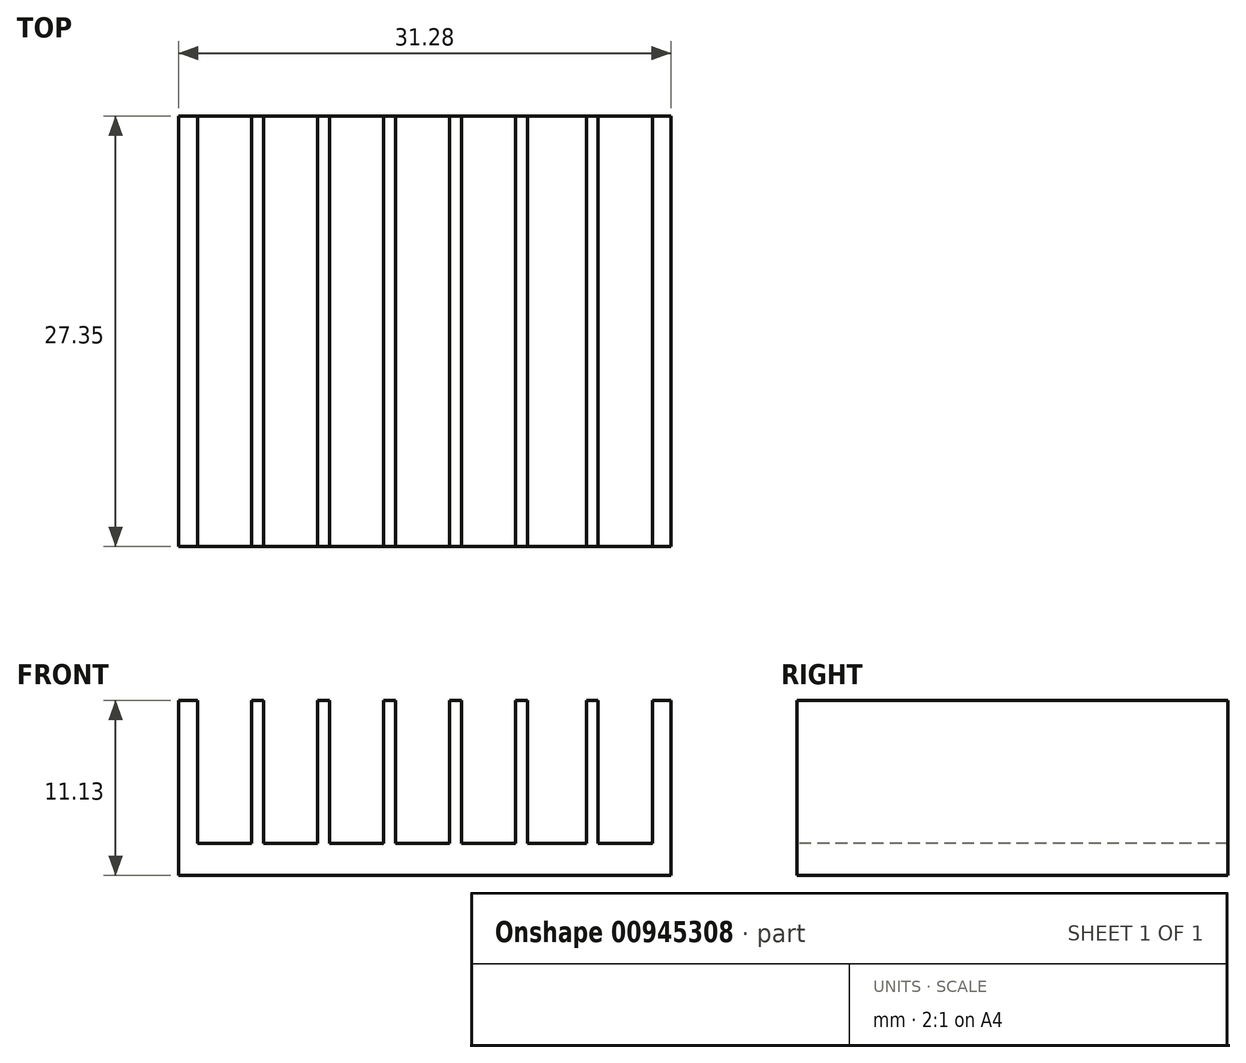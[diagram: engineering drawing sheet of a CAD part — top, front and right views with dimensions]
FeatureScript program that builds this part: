
annotation { "Feature Type Name" : "Feature", "Feature Type Description" : "" }
export const myFeature = defineFeature(function(context is Context, id is Id, definition is map)
    precondition{}
    {
        {
            var Q0;
            Q0=qCreatedBy(makeId("Top.planeOp"),FACE);
            var sketch = newSketch(context, id + "F0", { "sketchPlane" : qUnion([Q0])});
            skLineSegment(sketch, "E0", {"start": v(-31.28, 27.35) * mm, "end": v(0, 27.35) * mm});
            skLineSegment(sketch, "E1", {"start": v(0, 27.35) * mm, "end": v(0, 0) * mm});
            skLineSegment(sketch, "E2", {"start": v(0, 0) * mm, "end": v(-31.28, 0) * mm});
            skLineSegment(sketch, "E3", {"start": v(-31.28, 0) * mm, "end": v(-31.28, 27.35) * mm});
            skSolve(sketch);
        }
        {
            var Q0;
            Q0=makeQuery(id+"F0.imprint","IMPRINT",FACE,{"disambiguationData":[TD([[makeQuery(id+"F0.imprint","IMPRINT",EDGE,{"derivedFrom":sQuery(id+"F0.wireOp",EDGE,"E0")}),-1.0]])]});
            extrude(context, id + "F1", {"entities" : qUnion([Q0]), "depth" : 11.13 * mm, "offsetDistance" : 25.4 * mm});
        }
        {
            var Q0;
            Q0=makeQuery(id+"F1.opExtrude","SWEPT_FACE",FACE,{"disambiguationData":[OSD([sQuery(id+"F0.wireOp",EDGE,"E2")])]});
            var sketch = newSketch(context, id + "F2", { "sketchPlane" : qUnion([Q0])});
            skLineSegment(sketch, "E4", {"start": v(-30.09, 11.13) * mm, "end": v(-30.09, 2.04) * mm});
            skLineSegment(sketch, "E5", {"start": v(-30.09, 2.04) * mm, "end": v(-26.63, 2.04) * mm});
            skLineSegment(sketch, "E6", {"start": v(-26.63, 2.04) * mm, "end": v(-26.63, 11.13) * mm});
            skLineSegment(sketch, "E7", {"start": v(-1.2, 11.13) * mm, "end": v(-1.2, 2.04) * mm});
            skLineSegment(sketch, "E8", {"start": v(-1.2, 2.04) * mm, "end": v(-4.65, 2.04) * mm});
            skLineSegment(sketch, "E9", {"start": v(-4.65, 2.04) * mm, "end": v(-4.65, 11.13) * mm});
            skLineSegment(sketch, "E10", {"start": v(-25.9, 11.13) * mm, "end": v(-25.9, 2.03) * mm});
            skLineSegment(sketch, "E11", {"start": v(-25.9, 2.03) * mm, "end": v(-22.44, 2.03) * mm});
            skLineSegment(sketch, "E12", {"start": v(-22.44, 2.03) * mm, "end": v(-22.44, 11.13) * mm});
            skLineSegment(sketch, "E13", {"start": v(-21.7, 11.13) * mm, "end": v(-21.7, 2.03) * mm});
            skLineSegment(sketch, "E14", {"start": v(-21.7, 2.03) * mm, "end": v(-18.25, 2.03) * mm});
            skLineSegment(sketch, "E15", {"start": v(-18.25, 2.03) * mm, "end": v(-18.25, 11.13) * mm});
            skLineSegment(sketch, "E16", {"start": v(-17.51, 11.13) * mm, "end": v(-17.51, 2.03) * mm});
            skLineSegment(sketch, "E17", {"start": v(-17.51, 2.03) * mm, "end": v(-14.06, 2.03) * mm});
            skLineSegment(sketch, "E18", {"start": v(-14.06, 2.03) * mm, "end": v(-14.06, 11.13) * mm});
            skLineSegment(sketch, "E19", {"start": v(-13.32, 11.13) * mm, "end": v(-13.32, 2.03) * mm});
            skLineSegment(sketch, "E20", {"start": v(-13.32, 2.03) * mm, "end": v(-9.87, 2.03) * mm});
            skLineSegment(sketch, "E21", {"start": v(-9.87, 2.03) * mm, "end": v(-9.87, 11.13) * mm});
            skLineSegment(sketch, "E22", {"start": v(-9.13, 11.13) * mm, "end": v(-9.13, 2.03) * mm});
            skLineSegment(sketch, "E23", {"start": v(-9.13, 2.03) * mm, "end": v(-5.38, 2.03) * mm});
            skLineSegment(sketch, "E24", {"start": v(-5.38, 2.03) * mm, "end": v(-5.38, 11.13) * mm});
            skSolve(sketch);
        }
        {
            var Q0;
            {var subQ0=sQuery(id+"F2.wireOp",EDGE,"E10");Q0=makeQuery(id+"F2.imprint","IMPRINT",FACE,{"disambiguationData":[TD([[makeQuery(id+"F2.imprint","IMPRINT",EDGE,{"derivedFrom":subQ0}),1.0]])]});}
            var Q1;
            {var subQ0=sQuery(id+"F2.wireOp",EDGE,"E13");Q1=makeQuery(id+"F2.imprint","IMPRINT",FACE,{"disambiguationData":[TD([[makeQuery(id+"F2.imprint","IMPRINT",EDGE,{"derivedFrom":subQ0}),1.0]])]});}
            var Q2;
            {var subQ0=sQuery(id+"F2.wireOp",EDGE,"E16");Q2=makeQuery(id+"F2.imprint","IMPRINT",FACE,{"disambiguationData":[TD([[makeQuery(id+"F2.imprint","IMPRINT",EDGE,{"derivedFrom":subQ0}),1.0]])]});}
            var Q3;
            {var subQ0=sQuery(id+"F2.wireOp",EDGE,"E19");Q3=makeQuery(id+"F2.imprint","IMPRINT",FACE,{"disambiguationData":[TD([[makeQuery(id+"F2.imprint","IMPRINT",EDGE,{"derivedFrom":subQ0}),1.0]])]});}
            var Q4;
            {var subQ0=sQuery(id+"F2.wireOp",EDGE,"E22");Q4=makeQuery(id+"F2.imprint","IMPRINT",FACE,{"disambiguationData":[TD([[makeQuery(id+"F2.imprint","IMPRINT",EDGE,{"derivedFrom":subQ0}),1.0]])]});}
            var Q5;
            {var subQ0=sQuery(id+"F2.wireOp",EDGE,"E7");Q5=makeQuery(id+"F2.imprint","IMPRINT",FACE,{"disambiguationData":[TD([[makeQuery(id+"F2.imprint","IMPRINT",EDGE,{"derivedFrom":subQ0}),-1.0]])]});}
            var Q6;
            {var subQ0=sQuery(id+"F2.wireOp",EDGE,"E4");Q6=makeQuery(id+"F2.imprint","IMPRINT",FACE,{"disambiguationData":[TD([[makeQuery(id+"F2.imprint","IMPRINT",EDGE,{"derivedFrom":subQ0}),1.0]])]});}
            extrude(context, id + "F3", {"entities" : qUnion([Q0, Q1, Q2, Q3, Q4, Q5, Q6]), "operationType" : NewBodyOperationType.REMOVE, "endBound" : BoundingType.THROUGH_ALL, "oppositeDirection" : true, "depth" : 25.4 * mm, "offsetDistance" : 25.4 * mm});
        }
    });
